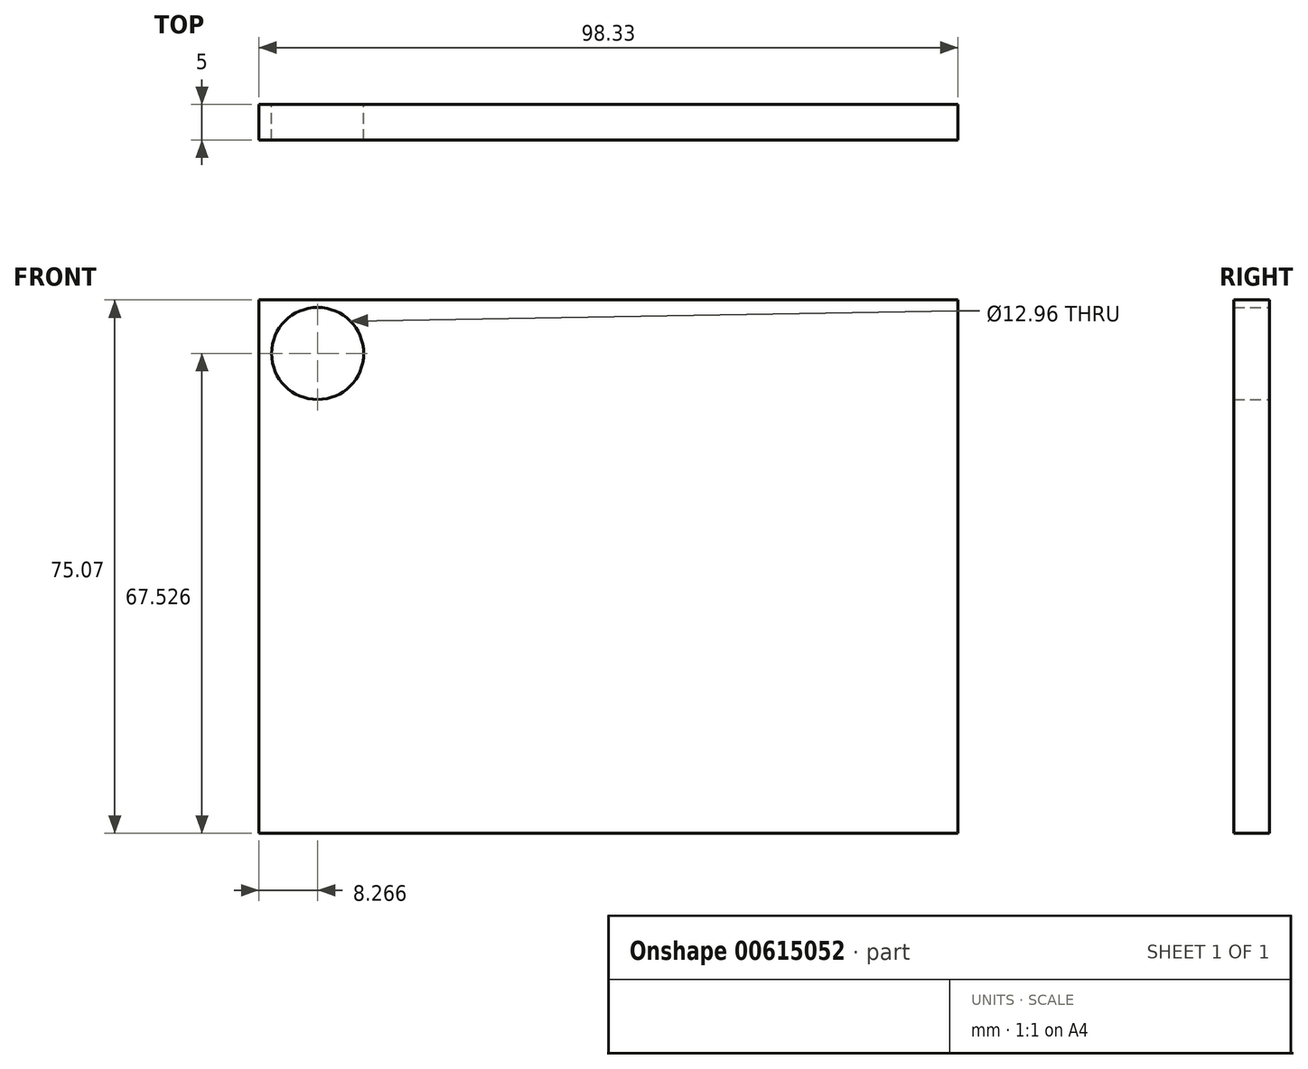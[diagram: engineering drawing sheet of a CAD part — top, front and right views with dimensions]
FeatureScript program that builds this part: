
annotation { "Feature Type Name" : "Feature", "Feature Type Description" : "" }
export const myFeature = defineFeature(function(context is Context, id is Id, definition is map)
    precondition{}
    {
        {
            var Q0;
            Q0=qCreatedBy(makeId("Front.planeOp"),FACE);
            var sketch = newSketch(context, id + "F0", { "sketchPlane" : qUnion([Q0])});
            skLineSegment(sketch, "E0.bottom", {"start": v(0, 0) * mm, "end": v(-98.33, 0) * mm});
            skLineSegment(sketch, "E0.top", {"start": v(0, 75.07) * mm, "end": v(-98.33, 75.07) * mm});
            skLineSegment(sketch, "E0.left", {"start": v(0, 0) * mm, "end": v(0, 75.07) * mm});
            skLineSegment(sketch, "E0.right", {"start": v(-98.33, 0) * mm, "end": v(-98.33, 75.07) * mm});
            skCircle(sketch, "E1", {"center": v(-90.06, 67.53) * mm, "radius": 6.48 * mm});
            skSolve(sketch);
        }
        {
            var Q0;
            Q0 = qSketchRegion(id + "F0", true);
            extrude(context, id + "F1", {"entities" : qUnion([Q0]), "depth" : 5 * mm, "offsetDistance" : 25 * mm});
        }
        {
            var Q0;
            Q0=qCreatedBy(makeId("Front.planeOp"),FACE);
            var sketch = newSketch(context, id + "F2", { "sketchPlane" : qUnion([Q0])});
            skText(sketch, "E2", { "text": "Nic", "fontName": "OpenSans-Italic.ttf"});
            const initialGuessF2  = {"E2": [-0.09617, 0.0282, 1, 0, 0.00988]};
            skSetInitialGuess(sketch, initialGuessF2);
            skSolve(sketch);
        }
        {
            var Q0;
            Q0 = qSketchRegion(id + "F2", true);
            extrude(context, id + "F3", {"entities" : qUnion([Q0]), "operationType" : NewBodyOperationType.ADD, "depth" : 5 * mm, "offsetDistance" : 25 * mm});
        }
        {
            var Q0;
            Q0 = qSketchRegion(id + "F2", true);
            extrude(context, id + "F4", {"entities" : qUnion([Q0]), "operationType" : NewBodyOperationType.ADD, "depth" : 3 * mm, "offsetDistance" : 25 * mm});
        }
        {
            var Q0;
            Q0 = qSketchRegion(id + "F2", true);
            extrude(context, id + "F5", {"entities" : qUnion([Q0]), "operationType" : NewBodyOperationType.ADD, "depth" : 5 * mm, "offsetDistance" : 25 * mm});
        }
    });
